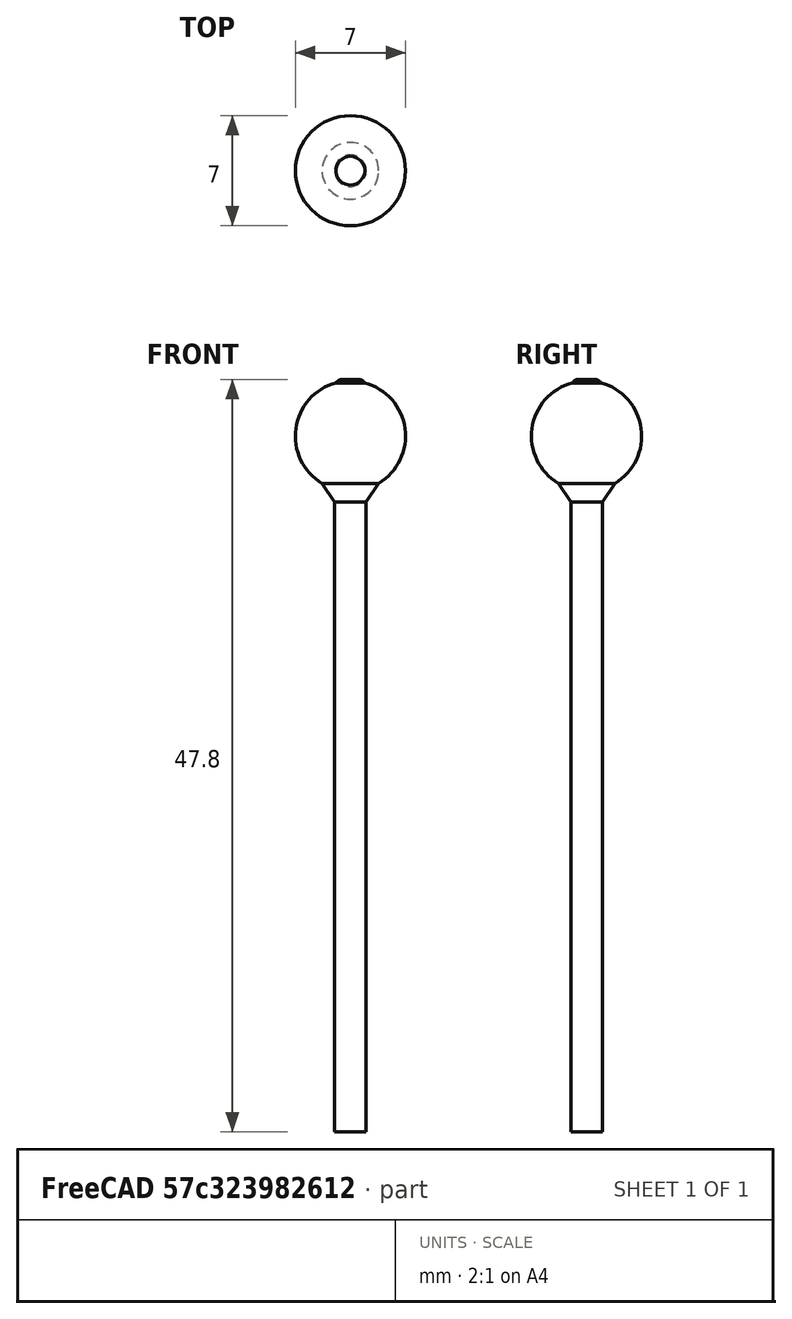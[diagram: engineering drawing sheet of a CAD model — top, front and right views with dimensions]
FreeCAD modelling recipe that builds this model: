
FCSTD DOCUMENT  (FreeCAD 0.18R4 (GitTag))
Label: Farola reto
License: All rights reserved
LicenseURL: http://en.wikipedia.org/wiki/All_rights_reserved
objects: Part::MultiFuse×3, Part::Cylinder×2, Part::Cone×1, Part::Sphere×1, Part::Fillet×1
note: 8 computed .brp shape members not serialized (recipe doc carries the construction recipe); baked Part::Feature solids carry a one-line shape summary decoded from their .brp

FEATURE [Part::Cylinder] Cylinder  label="Cilindro"
  Angle = 360
  AttacherType = Attacher::AttachEngine3D
  Height = 40
  Placement = pos=(0,0,-12) rot=(0,0,1;0rad)
  Radius = 1
FEATURE [Part::Cone] Cone  label="Cono"
  Angle = 360
  AttacherType = Attacher::AttachEngine3D
  Height = 3
  Placement = pos=(0,0,28) rot=(0,0,1;0rad)
  Radius1 = 1
  Radius2 = 3
FEATURE [Part::Sphere] Sphere  label="Esfera"
  Angle1 = -90
  Angle2 = 90
  Angle3 = 360
  AttacherType = Attacher::AttachEngine3D
  Placement = pos=(0,0,32.2) rot=(0,0,1;0rad)
  Radius = 3.5
FEATURE [Part::MultiFuse] Fusion
  Refine = true
  Shapes = -> [Cylinder,Cone]
FEATURE [Part::Cylinder] Cylinder001  label="Cilindro001"
  Angle = 360
  AttacherType = Attacher::AttachEngine3D
  Height = 10
  Placement = pos=(0,0,25.8) rot=(0,0,1;0rad)
  Radius = 1
FEATURE [Part::Fillet] Fillet
  Base = -> Cylinder001
  Edges = 1 edges r=0.5: [Edge1]
FEATURE [Part::MultiFuse] Fusion001
  Refine = true
  Shapes = -> [Fillet,Fusion]
FEATURE [Part::MultiFuse] Fusion002
  Refine = true
  Shapes = -> [Fusion001,Sphere]
